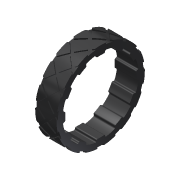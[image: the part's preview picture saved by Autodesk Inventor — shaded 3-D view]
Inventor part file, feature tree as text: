
AUTODESK INVENTOR PART (.ipt)
format: ipt  version: 2013 (Build 170138000, 138)  size: 928,768 bytes
history: native  units: in
note: dims shown in document units (in); Inventor stores cm internally (conversion verified against a paired STEP export)
features: extrude x1, mirror x1, imported_body x1, sketch x1
ambient origin geometry x8: Origin, YZ Plane, XZ Plane, XY Plane, X Axis, Y Axis, Z Axis, Center Point
bodies: Solid1 (feature_tree)
feature tree (4):
  extrude  "Extrusion1"  Depth=0.5in TaperAngle=0.0deg
  mirror  "Mirror1"
  imported_body  "Base1"
  sketch  "Sketch1"  dims[d0=4.5in d2=0.5in d3=0.0in]
